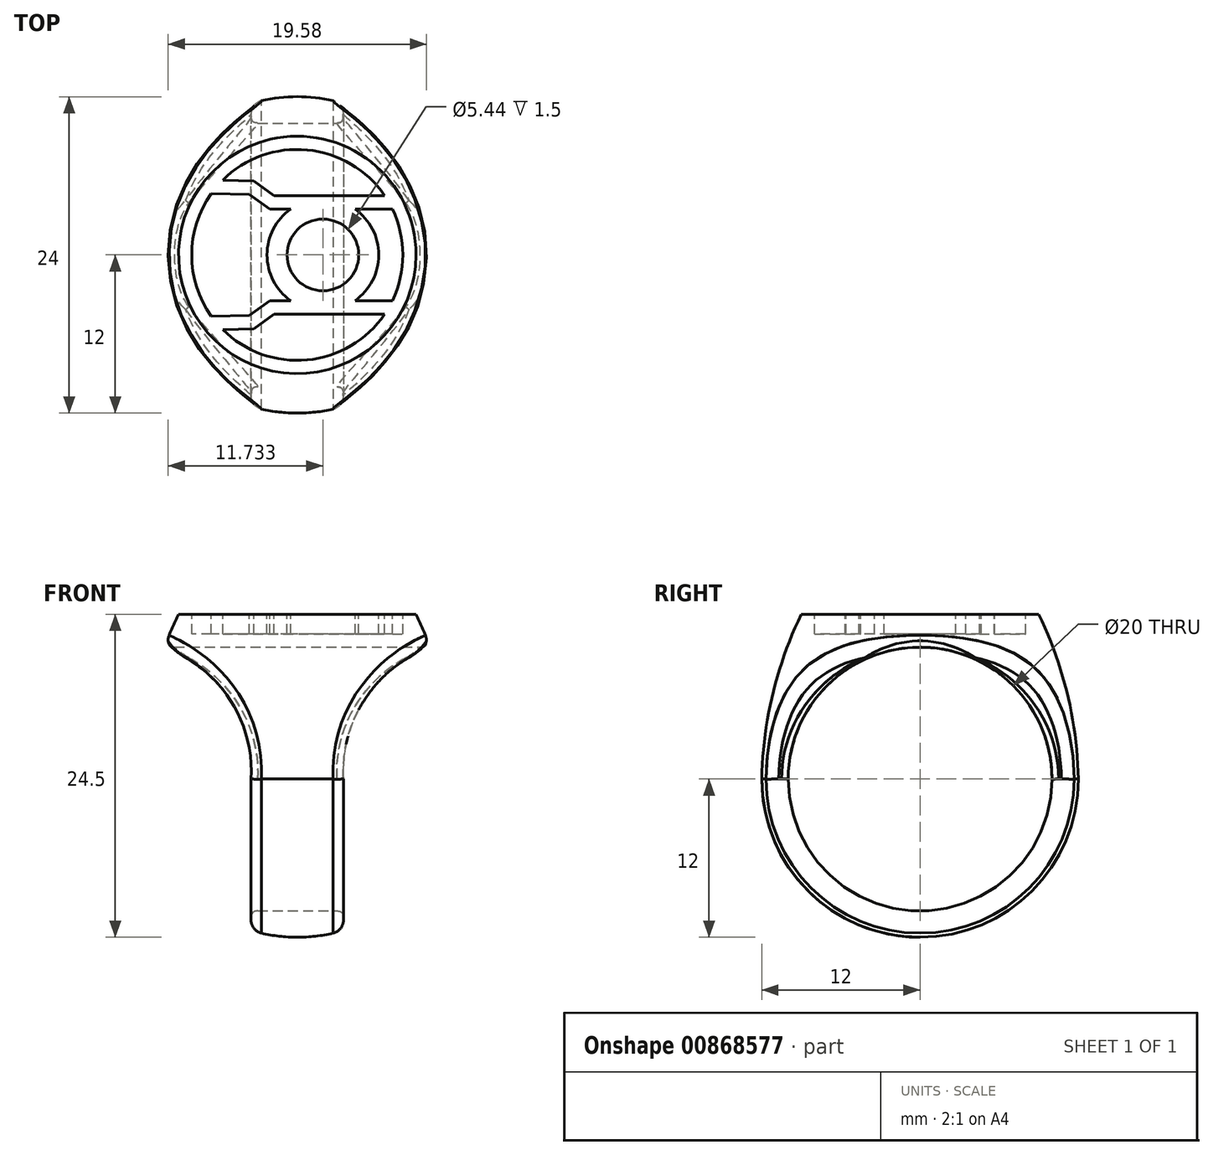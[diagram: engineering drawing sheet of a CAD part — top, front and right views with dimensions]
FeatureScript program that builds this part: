
annotation { "Feature Type Name" : "Feature", "Feature Type Description" : "" }
export const myFeature = defineFeature(function(context is Context, id is Id, definition is map)
    precondition{}
    {
        {
            var Q0;
            Q0=qCreatedBy(makeId("Right.planeOp"),FACE);
            var sketch = newSketch(context, id + "F0", { "sketchPlane" : qUnion([Q0])});
            skLineSegment(sketch, "E0", {"start": v(0, 0) * mm, "end": v(0, -24.5) * mm});
            skLineSegment(sketch, "E1", {"start": v(0, 0) * mm, "end": v(-9, 0) * mm});
            skArc(sketch, "E2", {"start": v(-12, -12.5) * mm, "mid": v(-8.49, -20.99) * mm, "end": v(0, -24.5) * mm});
            skLineSegment(sketch, "E3", {"start": v(0, -12.5) * mm, "end": v(-12, -12.5) * mm, "construction": true});
            skArc(sketch, "E4", {"start": v(-9, 0) * mm, "mid": v(-11.18, -6.09) * mm, "end": v(-12, -12.5) * mm});
            skSolve(sketch);
        }
        {
            var Q0;
            Q0=makeQuery(id+"F0.imprint","IMPRINT",FACE,{"disambiguationData":[TD([[makeQuery(id+"F0.imprint","IMPRINT",EDGE,{"derivedFrom":sQuery(id+"F0.wireOp",EDGE,"E0")}),-1.0]])]});
            var Q1;
            Q1=sQuery(id+"F0.wireOp",EDGE,"E0");
            revolve(context, id + "F1", {"entities" : qUnion([Q0]), "axis" : qUnion([Q1]), "revolveType" : RevolveType.FULL});
        }
        {
            var Q0;
            Q0=qCreatedBy(makeId("Right.planeOp"),FACE);
            var sketch = newSketch(context, id + "F2", { "sketchPlane" : qUnion([Q0])});
            skCircle(sketch, "E5", {"center": v(0, -12.5) * mm, "radius": 10 * mm});
            skSolve(sketch);
        }
        {
            var Q0;
            Q0=qSketchRegion(id+"F2",true);
            extrude(context, id + "F3", {"entities" : qUnion([Q0]), "operationType" : NewBodyOperationType.REMOVE, "endBound" : BoundingType.SYMMETRIC, "oppositeDirection" : true, "depth" : 25 * mm, "offsetDistance" : 25 * mm});
        }
        {
            var Q0;
            Q0=qCreatedBy(makeId("Front.planeOp"),FACE);
            var sketch = newSketch(context, id + "F4", { "sketchPlane" : qUnion([Q0])});
            skLineSegment(sketch, "E6", {"start": v(3.5, -26.5) * mm, "end": v(3.5, -12.5) * mm});
            skArc(sketch, "E7", {"start": v(10.15, -2.5) * mm, "mid": v(5.16, -6.39) * mm, "end": v(3.5, -12.5) * mm});
            skLineSegment(sketch, "E8", {"start": v(10.15, -2.5) * mm, "end": v(11.65, -2.5) * mm});
            skLineSegment(sketch, "E9", {"start": v(11.65, -2.5) * mm, "end": v(11.65, -26.5) * mm});
            skLineSegment(sketch, "E10", {"start": v(11.65, -26.5) * mm, "end": v(3.5, -26.5) * mm});
            skPoint(sketch, "E11.start.orphan", {"position": v(0, -24.5) * mm});
            skLineSegment(sketch, "E12", {"start": v(0, 0) * mm, "end": v(0, -24.5) * mm, "construction": true});
            skLineSegment(sketch, "E13.MirrorCS", {"start": v(-3.5, -26.5) * mm, "end": v(-3.5, -12.5) * mm});
            skArc(sketch, "E14.MirrorCS", {"start": v(-10.15, -2.5) * mm, "mid": v(-5.16, -6.39) * mm, "end": v(-3.5, -12.5) * mm});
            skLineSegment(sketch, "E15.MirrorCS", {"start": v(-11.65, -2.5) * mm, "end": v(-11.65, -26.5) * mm});
            skLineSegment(sketch, "E16.MirrorCS", {"start": v(-11.65, -26.5) * mm, "end": v(-3.5, -26.5) * mm});
            skLineSegment(sketch, "E17.MirrorCS", {"start": v(-10.15, -2.5) * mm, "end": v(-11.65, -2.5) * mm});
            skSolve(sketch);
        }
        {
            var Q0;
            Q0=qSketchRegion(id+"F4",true);
            extrude(context, id + "F5", {"entities" : qUnion([Q0]), "operationType" : NewBodyOperationType.REMOVE, "endBound" : BoundingType.SYMMETRIC, "depth" : 25 * mm, "offsetDistance" : 25 * mm});
        }
        {
            var Q0;
            Q0=makeQuery(id+"F1.opRevolve","SWEPT_FACE",FACE,{"disambiguationData":[OSD([sQuery(id+"F0.wireOp",EDGE,"E1")])]});
            var sketch = newSketch(context, id + "F6", { "sketchPlane" : qUnion([Q0])});
            skArc(sketch, "E18", {"start": v(-6.52, 4.64) * mm, "mid": v(-8, 0) * mm, "end": v(-6.52, -4.64) * mm});
            skLineSegment(sketch, "E19", {"start": v(-8, 0) * mm, "end": v(8, 0) * mm, "construction": true});
            skArc(sketch, "E20", {"start": v(4.66, 0) * mm, "mid": v(1.94, 2.72) * mm, "end": v(-0.77, 0) * mm});
            skArc(sketch, "E21", {"start": v(-0.5, 3.46) * mm, "mid": v(-1.82, 1.95) * mm, "end": v(-2.3, 0) * mm});
            skLineSegment(sketch, "E22", {"start": v(6.61, 4.5) * mm, "end": v(-1.75, 4.5) * mm});
            skLineSegment(sketch, "E23", {"start": v(-1.75, 4.5) * mm, "end": v(-3.3, 5.61) * mm});
            skLineSegment(sketch, "E24", {"start": v(-3.3, 5.61) * mm, "end": v(-5.65, 5.66) * mm});
            skLineSegment(sketch, "E25", {"start": v(7.21, 3.46) * mm, "end": v(4.38, 3.46) * mm});
            skLineSegment(sketch, "E26", {"start": v(-2.09, 3.46) * mm, "end": v(-3.64, 4.58) * mm});
            skLineSegment(sketch, "E27", {"start": v(-3.64, 4.58) * mm, "end": v(-6.52, 4.64) * mm});
            skLineSegment(sketch, "E28.trimOffspring", {"start": v(-0.5, 3.46) * mm, "end": v(-2.09, 3.46) * mm});
            skArc(sketch, "E29.trimOffspring", {"start": v(6.18, 0) * mm, "mid": v(5.7, 1.95) * mm, "end": v(4.38, 3.46) * mm});
            skArc(sketch, "E30.trimOffspring", {"start": v(6.61, 4.5) * mm, "mid": v(0.75, 7.96) * mm, "end": v(-5.65, 5.66) * mm});
            skLineSegment(sketch, "E31.MirrorCS", {"start": v(7.21, -3.46) * mm, "end": v(4.38, -3.46) * mm});
            skArc(sketch, "E32.MirrorCS", {"start": v(6.18, 0) * mm, "mid": v(5.7, -1.95) * mm, "end": v(4.38, -3.46) * mm});
            skArc(sketch, "E33.MirrorCS", {"start": v(4.66, 0) * mm, "mid": v(1.94, -2.72) * mm, "end": v(-0.77, 0) * mm});
            skArc(sketch, "E34.MirrorCS", {"start": v(-0.5, -3.46) * mm, "mid": v(-1.82, -1.95) * mm, "end": v(-2.3, 0) * mm});
            skLineSegment(sketch, "E35.MirrorCS", {"start": v(-0.5, -3.46) * mm, "end": v(-2.09, -3.46) * mm});
            skLineSegment(sketch, "E36.MirrorCS", {"start": v(6.61, -4.5) * mm, "end": v(-1.75, -4.5) * mm});
            skLineSegment(sketch, "E37.MirrorCS", {"start": v(-1.75, -4.5) * mm, "end": v(-3.3, -5.61) * mm});
            skLineSegment(sketch, "E38.MirrorCS", {"start": v(-2.09, -3.46) * mm, "end": v(-3.64, -4.58) * mm});
            skLineSegment(sketch, "E39.MirrorCS", {"start": v(-3.3, -5.61) * mm, "end": v(-5.65, -5.66) * mm});
            skLineSegment(sketch, "E40.MirrorCS", {"start": v(-3.64, -4.58) * mm, "end": v(-6.52, -4.64) * mm});
            skArc(sketch, "E41.trimOffspring", {"start": v(-5.65, -5.66) * mm, "mid": v(0.75, -7.96) * mm, "end": v(6.61, -4.5) * mm});
            skArc(sketch, "E42.trimOffspring", {"start": v(7.21, -3.46) * mm, "mid": v(8, 0) * mm, "end": v(7.21, 3.46) * mm});
            skSolve(sketch);
        }
        {
            var Q0;
            Q0=qSketchRegion(id+"F6",true);
            var Q1;
            Q1=makeQuery(id+"F6.imprint","IMPRINT",FACE,{"disambiguationData":[TD([[makeQuery(id+"F6.imprint","IMPRINT",EDGE,{"derivedFrom":sQuery(id+"F6.wireOp",EDGE,"g20j87Mm-wGr7-AMiz-bI8b-qS7GuHKO57cL")}),1.0]])]});
            extrude(context, id + "F7", {"entities" : qUnion([Q0, Q1]), "operationType" : NewBodyOperationType.REMOVE, "oppositeDirection" : true, "depth" : 1.5 * mm, "offsetDistance" : 25 * mm});
        }
        {
            var Q0;
            Q0=makeQuery(id+"F5.boolean.opBoolean","INTERSECT",EDGE,{"disambiguationData":[OD(1.0)],"derivedFrom":[makeQuery(id+"F1.opRevolve","SWEPT_FACE",FACE,{"disambiguationData":[OSD([sQuery(id+"F0.wireOp",EDGE,"E4")])]}),makeQuery(id+"F5.opExtrude","SWEPT_FACE",FACE,{"disambiguationData":[OSD([sQuery(id+"F4.wireOp",EDGE,"E14.MirrorCS")])]})]});
            var Q1;
            Q1=makeQuery(id+"F5.boolean.opBoolean","INTERSECT",EDGE,{"derivedFrom":[makeQuery(id+"F1.opRevolve","SWEPT_FACE",FACE,{"disambiguationData":[OSD([sQuery(id+"F0.wireOp",EDGE,"E2")])]}),makeQuery(id+"F5.opExtrude","SWEPT_FACE",FACE,{"disambiguationData":[OSD([sQuery(id+"F4.wireOp",EDGE,"E13.MirrorCS")])]})]});
            var Q2;
            Q2=makeQuery(id+"F5.boolean.opBoolean","INTERSECT",EDGE,{"disambiguationData":[OD(1.0)],"derivedFrom":[makeQuery(id+"F1.opRevolve","SWEPT_FACE",FACE,{"disambiguationData":[OSD([sQuery(id+"F0.wireOp",EDGE,"E4")])]}),makeQuery(id+"F5.opExtrude","SWEPT_FACE",FACE,{"disambiguationData":[OSD([sQuery(id+"F4.wireOp",EDGE,"E7")])]})]});
            var Q3;
            Q3=makeQuery(id+"F5.boolean.opBoolean","INTERSECT",EDGE,{"derivedFrom":[makeQuery(id+"F1.opRevolve","SWEPT_FACE",FACE,{"disambiguationData":[OSD([sQuery(id+"F0.wireOp",EDGE,"E2")])]}),makeQuery(id+"F5.opExtrude","SWEPT_FACE",FACE,{"disambiguationData":[OSD([sQuery(id+"F4.wireOp",EDGE,"E6")])]})]});
            fillet(context, id + "F8", {"entities" : qUnion([Q0, Q1, Q2, Q3]), "radius" : 1 * mm, "allowEdgeOverflow" : false});
        }
        {
            var Q0;
            Q0=makeQuery(id+"F5.boolean.opBoolean","INTERSECT",EDGE,{"disambiguationData":[OD(1.0)],"derivedFrom":[makeQuery(id+"F3.boolean.opBoolean","COPY",FACE,{"derivedFrom":makeQuery(id+"F3.opExtrude","SWEPT_FACE",FACE,{"disambiguationData":[OSD([sQuery(id+"F2.wireOp",EDGE,"E5")])]})}),makeQuery(id+"F5.opExtrude","SWEPT_FACE",FACE,{"disambiguationData":[OSD([sQuery(id+"F4.wireOp",EDGE,"E14.MirrorCS")])]})]});
            var Q1;
            Q1=makeQuery(id+"F5.boolean.opBoolean","INTERSECT",EDGE,{"derivedFrom":[makeQuery(id+"F3.boolean.opBoolean","COPY",FACE,{"derivedFrom":makeQuery(id+"F3.opExtrude","SWEPT_FACE",FACE,{"disambiguationData":[OSD([sQuery(id+"F2.wireOp",EDGE,"E5")])]})}),makeQuery(id+"F5.opExtrude","SWEPT_FACE",FACE,{"disambiguationData":[OSD([sQuery(id+"F4.wireOp",EDGE,"E13.MirrorCS")])]})]});
            var Q2;
            Q2=makeQuery(id+"F5.boolean.opBoolean","INTERSECT",EDGE,{"disambiguationData":[OD(0.0)],"derivedFrom":[makeQuery(id+"F3.boolean.opBoolean","COPY",FACE,{"derivedFrom":makeQuery(id+"F3.opExtrude","SWEPT_FACE",FACE,{"disambiguationData":[OSD([sQuery(id+"F2.wireOp",EDGE,"E5")])]})}),makeQuery(id+"F5.opExtrude","SWEPT_FACE",FACE,{"disambiguationData":[OSD([sQuery(id+"F4.wireOp",EDGE,"E14.MirrorCS")])]})]});
            var Q3;
            Q3=makeQuery(id+"F5.boolean.opBoolean","INTERSECT",EDGE,{"disambiguationData":[OD(0.0)],"derivedFrom":[makeQuery(id+"F3.boolean.opBoolean","COPY",FACE,{"derivedFrom":makeQuery(id+"F3.opExtrude","SWEPT_FACE",FACE,{"disambiguationData":[OSD([sQuery(id+"F2.wireOp",EDGE,"E5")])]})}),makeQuery(id+"F5.opExtrude","SWEPT_FACE",FACE,{"disambiguationData":[OSD([sQuery(id+"F4.wireOp",EDGE,"E7")])]})]});
            var Q4;
            Q4=makeQuery(id+"F3.boolean.opBoolean","COPY",FACE,{"derivedFrom":makeQuery(id+"F3.opExtrude","SWEPT_FACE",FACE,{"disambiguationData":[OSD([sQuery(id+"F2.wireOp",EDGE,"E5")])]})});
            fillet(context, id + "F9", {"entities" : qUnion([Q0, Q1, Q2, Q3, Q4]), "radius" : .5 * mm, "rho" : 0.5, "crossSection" : FilletCrossSection.CONIC, "allowEdgeOverflow" : false});
        }
    });
